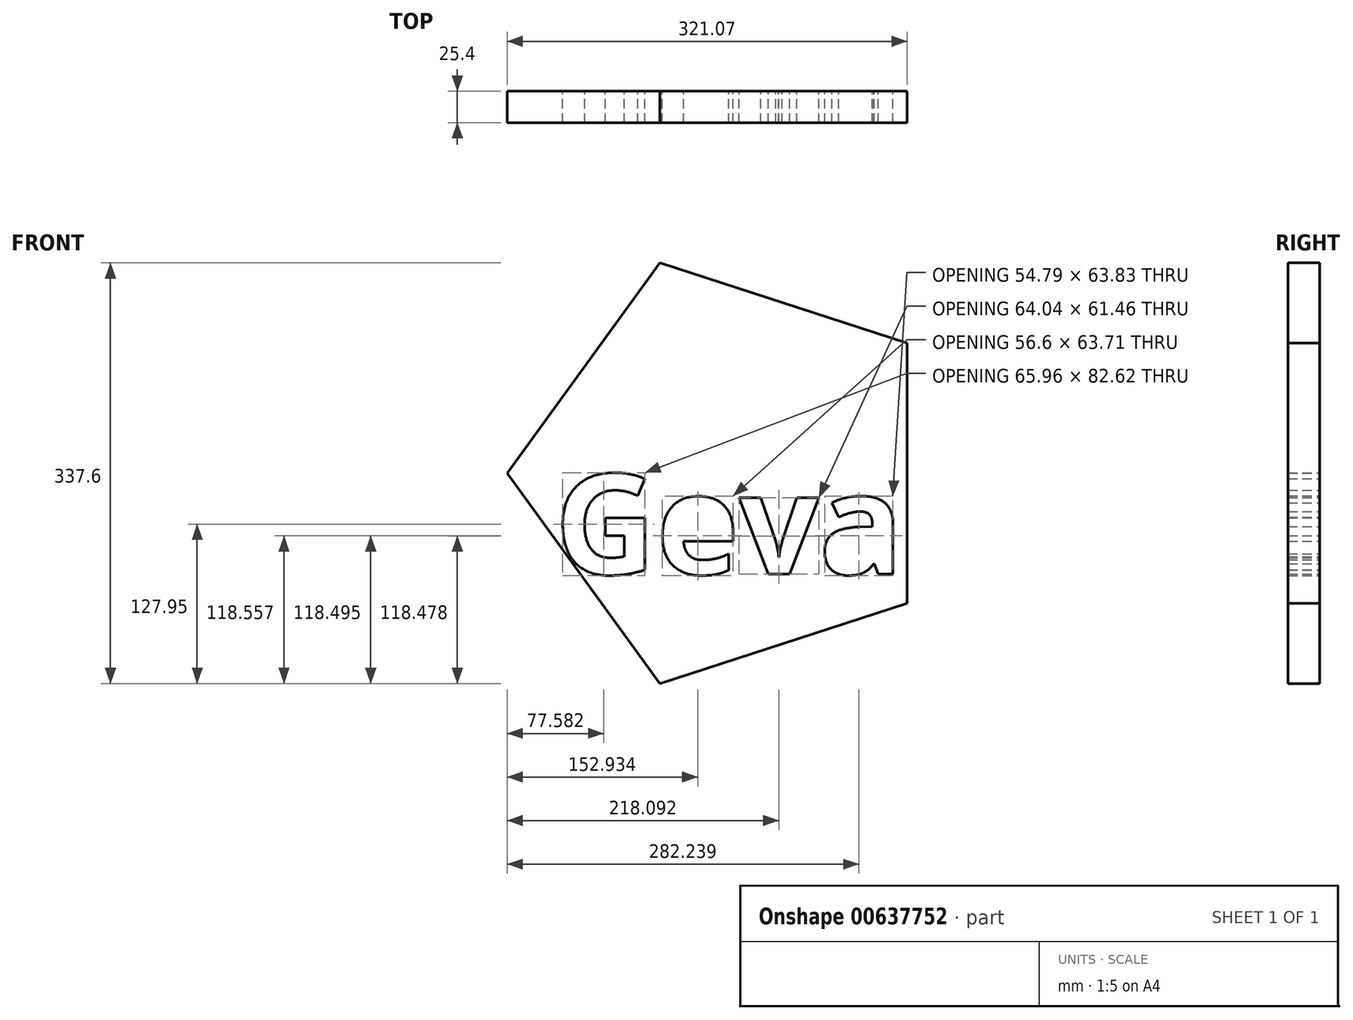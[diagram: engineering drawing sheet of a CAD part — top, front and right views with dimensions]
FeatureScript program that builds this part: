
annotation { "Feature Type Name" : "Feature", "Feature Type Description" : "" }
export const myFeature = defineFeature(function(context is Context, id is Id, definition is map)
    precondition{}
    {
        {
            var Q0;
            Q0=qCreatedBy(makeId("Front.planeOp"),FACE);
            var sketch = newSketch(context, id + "F0", { "sketchPlane" : qUnion([Q0])});
            skText(sketch, "E0", { "text": "Geva", "fontName": "OpenSans-Bold.ttf"});
            skCircle(sketch, "E1.cCircle", {"center": v(-14.8, 44.42) * mm, "radius": 177.48 * mm, "construction": true});
            skLineSegment(sketch, "E1.0", {"start": v(-192.29, 44.42) * mm, "end": v(-69.65, 213.22) * mm});
            skLineSegment(sketch, "E1.1", {"start": v(-69.65, 213.22) * mm, "end": v(128.78, 148.74) * mm});
            skLineSegment(sketch, "E1.2", {"start": v(128.78, 148.74) * mm, "end": v(128.78, -59.9) * mm});
            skLineSegment(sketch, "E1.3", {"start": v(128.78, -59.9) * mm, "end": v(-69.65, -124.38) * mm});
            skLineSegment(sketch, "E1.4", {"start": v(-69.65, -124.38) * mm, "end": v(-192.29, 44.42) * mm});
            const initialGuessF0  = {"E0": [-0.15423, -0.03663, 1, 0, 0.08105]};
            skSetInitialGuess(sketch, initialGuessF0);
            skSolve(sketch);
        }
        {
            var Q0;
            Q0 = qSketchRegion(id + "F0", true);
            extrude(context, id + "F1", {"entities" : qUnion([Q0]), "depth" : 25.4 * mm, "offsetDistance" : 25.4 * mm});
        }
    });
